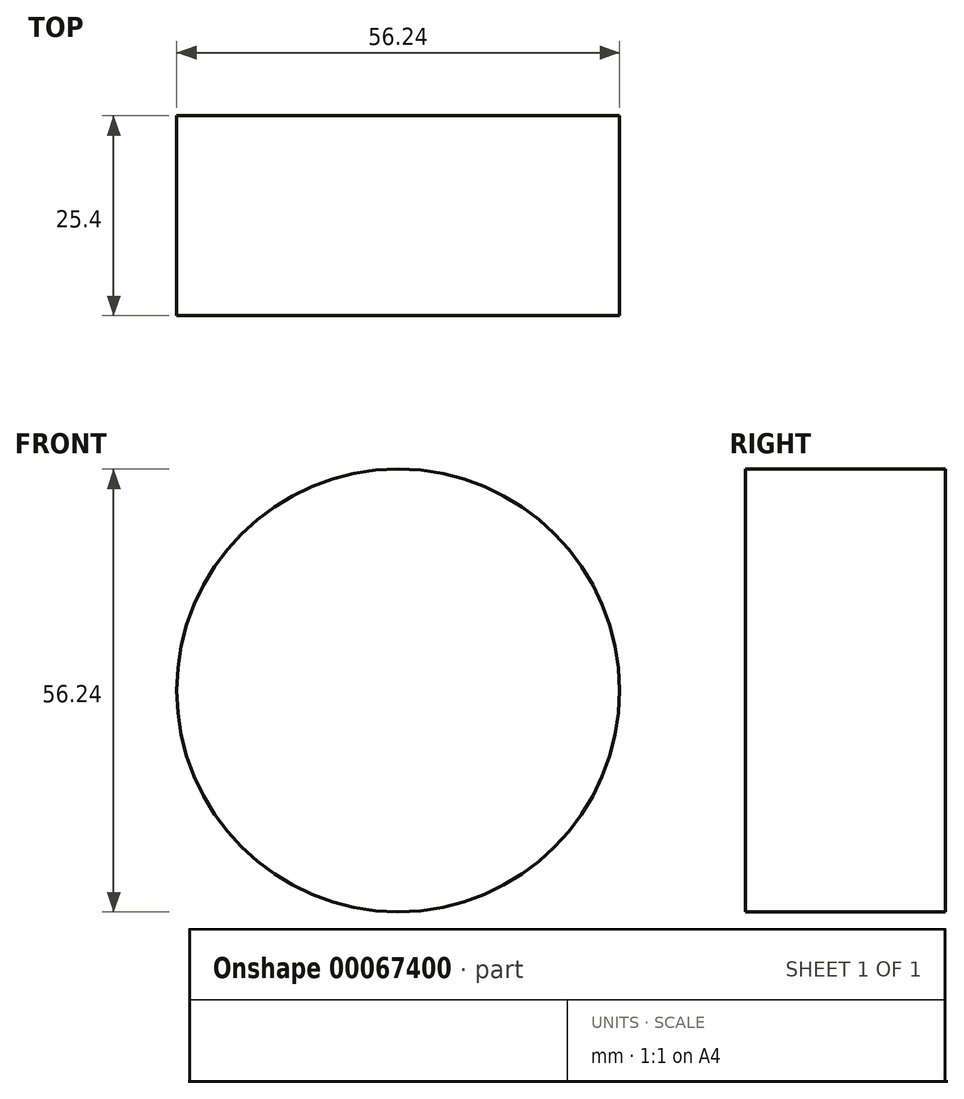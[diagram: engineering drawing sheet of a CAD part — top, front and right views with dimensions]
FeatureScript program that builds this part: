
annotation { "Feature Type Name" : "Feature", "Feature Type Description" : "" }
export const myFeature = defineFeature(function(context is Context, id is Id, definition is map)
    precondition{}
    {
        {
            var Q0;
            Q0=qCreatedBy(makeId("Front.planeOp"),FACE);
            var sketch = newSketch(context, id + "F0", { "sketchPlane" : qUnion([Q0])});
            skCircle(sketch, "E0", {"center": v(-3.79, -2.75) * mm, "radius": 28.12 * mm});
            skSolve(sketch);
        }
        {
            var Q0;
            Q0 = qSketchRegion(id + "F0", true);
            extrude(context, id + "F1", {"entities" : qUnion([Q0]), "depth" : 25.4 * mm});
        }
    });
